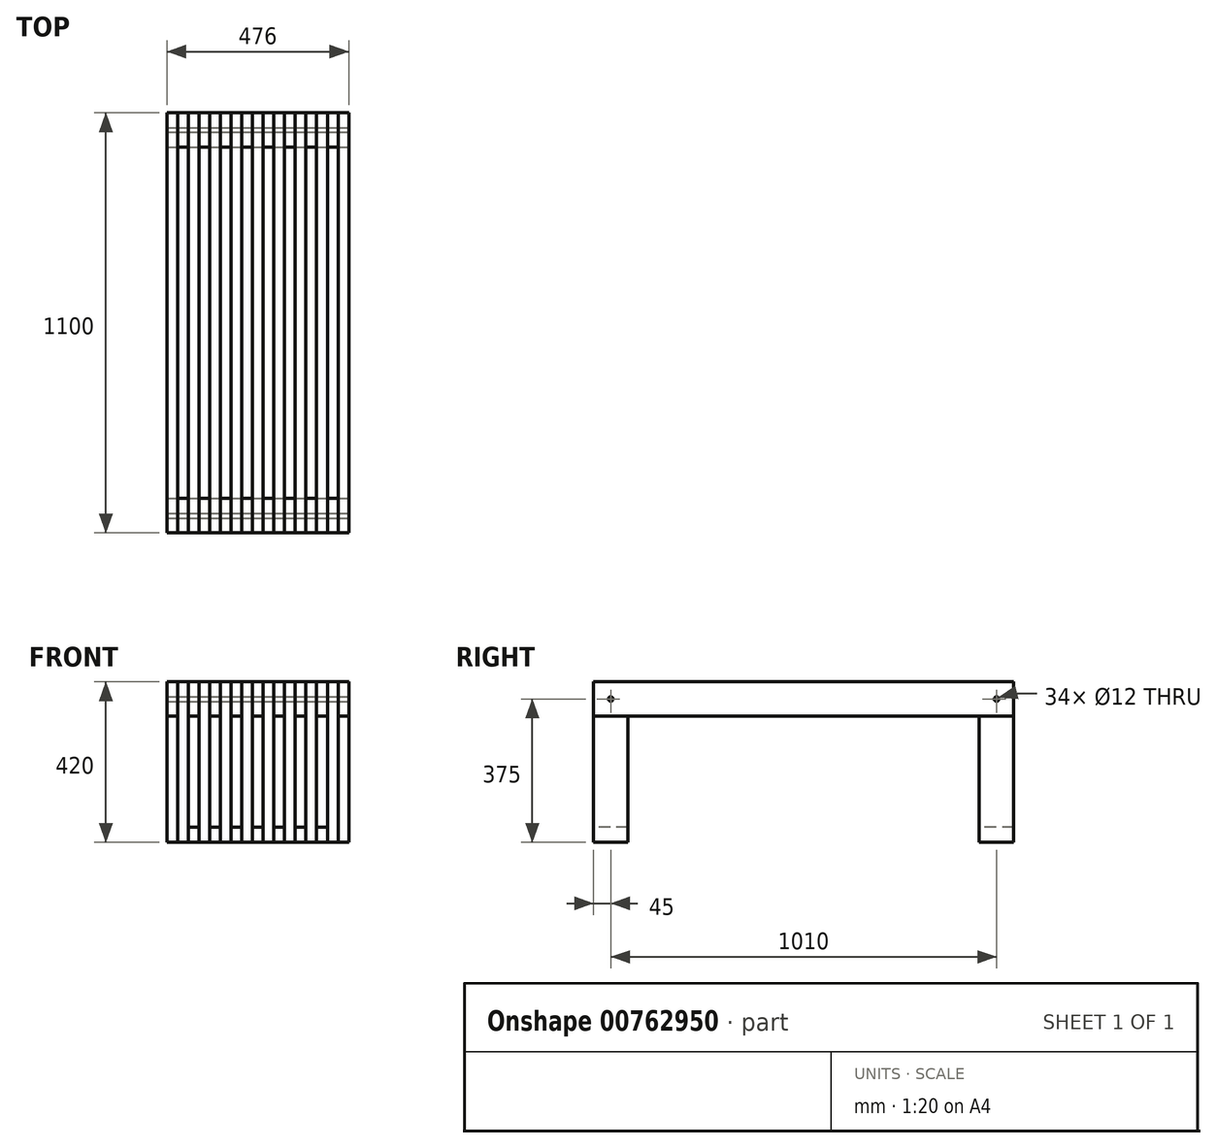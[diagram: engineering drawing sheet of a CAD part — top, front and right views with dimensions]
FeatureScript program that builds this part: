
annotation { "Feature Type Name" : "Feature", "Feature Type Description" : "" }
export const myFeature = defineFeature(function(context is Context, id is Id, definition is map)
    precondition{}
    {
        {
            var Q0;
            Q0=qCreatedBy(makeId("Front.planeOp"),FACE);
            var sketch = newSketch(context, id + "F0", { "sketchPlane" : qUnion([Q0])});
            skLineSegment(sketch, "E0.bottom", {"start": v(0, 0) * mm, "end": v(28, 0) * mm});
            skLineSegment(sketch, "E0.top", {"start": v(0, 90) * mm, "end": v(28, 90) * mm});
            skLineSegment(sketch, "E0.left", {"start": v(0, 0) * mm, "end": v(0, 90) * mm});
            skLineSegment(sketch, "E0.right", {"start": v(28, 0) * mm, "end": v(28, 90) * mm});
            skLineSegment(sketch, "E1.1.0.0", {"start": v(56, 90) * mm, "end": v(84, 90) * mm});
            skLineSegment(sketch, "E1.1.0.1", {"start": v(56, 0) * mm, "end": v(56, 90) * mm});
            skLineSegment(sketch, "E1.1.0.2", {"start": v(84, 0) * mm, "end": v(84, 90) * mm});
            skLineSegment(sketch, "E1.1.0.3", {"start": v(56, 0) * mm, "end": v(84, 0) * mm});
            skLineSegment(sketch, "E1.2.0.0", {"start": v(112, 90) * mm, "end": v(140, 90) * mm});
            skLineSegment(sketch, "E1.2.0.1", {"start": v(112, 0) * mm, "end": v(112, 90) * mm});
            skLineSegment(sketch, "E1.2.0.2", {"start": v(140, 0) * mm, "end": v(140, 90) * mm});
            skLineSegment(sketch, "E1.2.0.3", {"start": v(112, 0) * mm, "end": v(140, 0) * mm});
            skLineSegment(sketch, "E1.3.0.0", {"start": v(168, 90) * mm, "end": v(196, 90) * mm});
            skLineSegment(sketch, "E1.3.0.1", {"start": v(168, 0) * mm, "end": v(168, 90) * mm});
            skLineSegment(sketch, "E1.3.0.2", {"start": v(196, 0) * mm, "end": v(196, 90) * mm});
            skLineSegment(sketch, "E1.3.0.3", {"start": v(168, 0) * mm, "end": v(196, 0) * mm});
            skLineSegment(sketch, "E1.4.0.0", {"start": v(224, 90) * mm, "end": v(252, 90) * mm});
            skLineSegment(sketch, "E1.4.0.1", {"start": v(224, 0) * mm, "end": v(224, 90) * mm});
            skLineSegment(sketch, "E1.4.0.2", {"start": v(252, 0) * mm, "end": v(252, 90) * mm});
            skLineSegment(sketch, "E1.4.0.3", {"start": v(224, 0) * mm, "end": v(252, 0) * mm});
            skLineSegment(sketch, "E1.5.0.0", {"start": v(280, 90) * mm, "end": v(308, 90) * mm});
            skLineSegment(sketch, "E1.5.0.1", {"start": v(280, 0) * mm, "end": v(280, 90) * mm});
            skLineSegment(sketch, "E1.5.0.2", {"start": v(308, 0) * mm, "end": v(308, 90) * mm});
            skLineSegment(sketch, "E1.5.0.3", {"start": v(280, 0) * mm, "end": v(308, 0) * mm});
            skLineSegment(sketch, "E1.6.0.0", {"start": v(336, 90) * mm, "end": v(364, 90) * mm});
            skLineSegment(sketch, "E1.6.0.1", {"start": v(336, 0) * mm, "end": v(336, 90) * mm});
            skLineSegment(sketch, "E1.6.0.2", {"start": v(364, 0) * mm, "end": v(364, 90) * mm});
            skLineSegment(sketch, "E1.6.0.3", {"start": v(336, 0) * mm, "end": v(364, 0) * mm});
            skLineSegment(sketch, "E1.7.0.0", {"start": v(392, 90) * mm, "end": v(420, 90) * mm});
            skLineSegment(sketch, "E1.7.0.1", {"start": v(392, 0) * mm, "end": v(392, 90) * mm});
            skLineSegment(sketch, "E1.7.0.2", {"start": v(420, 0) * mm, "end": v(420, 90) * mm});
            skLineSegment(sketch, "E1.7.0.3", {"start": v(392, 0) * mm, "end": v(420, 0) * mm});
            skLineSegment(sketch, "E1.direction1", {"start": v(0, 0) * mm, "end": v(56, 0) * mm, "construction": true});
            skLineSegment(sketch, "E2.0.8.0", {"start": v(448, 90) * mm, "end": v(476, 90) * mm});
            skLineSegment(sketch, "E2.3.8.0", {"start": v(448, 0) * mm, "end": v(448, 90) * mm});
            skLineSegment(sketch, "E2.6.8.0", {"start": v(476, 0) * mm, "end": v(476, 90) * mm});
            skLineSegment(sketch, "E2.9.8.0", {"start": v(448, 0) * mm, "end": v(476, 0) * mm});
            skSolve(sketch);
        }
        {
            var Q0;
            Q0=makeQuery(id+"F0.imprint","IMPRINT",FACE,{"disambiguationData":[TD([[makeQuery(id+"F0.imprint","IMPRINT",EDGE,{"derivedFrom":sQuery(id+"F0.wireOp",EDGE,"E0.bottom")}),1.0]])]});
            var Q1;
            Q1=makeQuery(id+"F0.imprint","IMPRINT",FACE,{"disambiguationData":[TD([[makeQuery(id+"F0.imprint","IMPRINT",EDGE,{"derivedFrom":sQuery(id+"F0.wireOp",EDGE,"E1.1.0.0")}),-1.0]])]});
            var Q2;
            Q2=makeQuery(id+"F0.imprint","IMPRINT",FACE,{"disambiguationData":[TD([[makeQuery(id+"F0.imprint","IMPRINT",EDGE,{"derivedFrom":sQuery(id+"F0.wireOp",EDGE,"E1.2.0.0")}),-1.0]])]});
            var Q3;
            Q3=makeQuery(id+"F0.imprint","IMPRINT",FACE,{"disambiguationData":[TD([[makeQuery(id+"F0.imprint","IMPRINT",EDGE,{"derivedFrom":sQuery(id+"F0.wireOp",EDGE,"E1.3.0.0")}),-1.0]])]});
            var Q4;
            Q4=makeQuery(id+"F0.imprint","IMPRINT",FACE,{"disambiguationData":[TD([[makeQuery(id+"F0.imprint","IMPRINT",EDGE,{"derivedFrom":sQuery(id+"F0.wireOp",EDGE,"E1.4.0.0")}),-1.0]])]});
            var Q5;
            Q5=makeQuery(id+"F0.imprint","IMPRINT",FACE,{"disambiguationData":[TD([[makeQuery(id+"F0.imprint","IMPRINT",EDGE,{"derivedFrom":sQuery(id+"F0.wireOp",EDGE,"E1.5.0.0")}),-1.0]])]});
            var Q6;
            Q6=makeQuery(id+"F0.imprint","IMPRINT",FACE,{"disambiguationData":[TD([[makeQuery(id+"F0.imprint","IMPRINT",EDGE,{"derivedFrom":sQuery(id+"F0.wireOp",EDGE,"E1.6.0.0")}),-1.0]])]});
            var Q7;
            Q7=makeQuery(id+"F0.imprint","IMPRINT",FACE,{"disambiguationData":[TD([[makeQuery(id+"F0.imprint","IMPRINT",EDGE,{"derivedFrom":sQuery(id+"F0.wireOp",EDGE,"E1.7.0.0")}),-1.0]])]});
            var Q8;
            Q8=makeQuery(id+"F0.imprint","IMPRINT",FACE,{"disambiguationData":[TD([[makeQuery(id+"F0.imprint","IMPRINT",EDGE,{"derivedFrom":sQuery(id+"F0.wireOp",EDGE,"E2.0.8.0")}),-1.0]])]});
            extrude(context, id + "F1", {"entities" : qUnion([Q0, Q1, Q2, Q3, Q4, Q5, Q6, Q7, Q8]), "depth" : 1100 * mm, "offsetDistance" : 25 * mm});
        }
        {
            var Q0;
            Q0=qCreatedBy(makeId("Top.planeOp"),FACE);
            var sketch = newSketch(context, id + "F2", { "sketchPlane" : qUnion([Q0])});
            skLineSegment(sketch, "E3.bottom", {"start": v(28, 0) * mm, "end": v(56, 0) * mm});
            skLineSegment(sketch, "E3.top", {"start": v(28, -90) * mm, "end": v(56, -90) * mm});
            skLineSegment(sketch, "E3.left", {"start": v(28, 0) * mm, "end": v(28, -90) * mm});
            skLineSegment(sketch, "E3.right", {"start": v(56, 0) * mm, "end": v(56, -90) * mm});
            skLineSegment(sketch, "E4.0.1.0", {"start": v(28, -1010) * mm, "end": v(56, -1010) * mm});
            skLineSegment(sketch, "E4.0.1.1", {"start": v(28, -1100) * mm, "end": v(56, -1100) * mm});
            skLineSegment(sketch, "E4.0.1.2", {"start": v(28, -1010) * mm, "end": v(28, -1100) * mm});
            skLineSegment(sketch, "E4.0.1.3", {"start": v(56, -1010) * mm, "end": v(56, -1100) * mm});
            skLineSegment(sketch, "E4.1.0.0", {"start": v(84, 0) * mm, "end": v(112, 0) * mm});
            skLineSegment(sketch, "E4.1.0.1", {"start": v(84, -90) * mm, "end": v(112, -90) * mm});
            skLineSegment(sketch, "E4.1.0.2", {"start": v(84, 0) * mm, "end": v(84, -90) * mm});
            skLineSegment(sketch, "E4.1.0.3", {"start": v(112, 0) * mm, "end": v(112, -90) * mm});
            skLineSegment(sketch, "E4.1.1.0", {"start": v(84, -1010) * mm, "end": v(112, -1010) * mm});
            skLineSegment(sketch, "E4.1.1.1", {"start": v(84, -1100) * mm, "end": v(112, -1100) * mm});
            skLineSegment(sketch, "E4.1.1.2", {"start": v(84, -1010) * mm, "end": v(84, -1100) * mm});
            skLineSegment(sketch, "E4.1.1.3", {"start": v(112, -1010) * mm, "end": v(112, -1100) * mm});
            skLineSegment(sketch, "E4.2.0.0", {"start": v(140, 0) * mm, "end": v(168, 0) * mm});
            skLineSegment(sketch, "E4.2.0.1", {"start": v(140, -90) * mm, "end": v(168, -90) * mm});
            skLineSegment(sketch, "E4.2.0.2", {"start": v(140, 0) * mm, "end": v(140, -90) * mm});
            skLineSegment(sketch, "E4.2.0.3", {"start": v(168, 0) * mm, "end": v(168, -90) * mm});
            skLineSegment(sketch, "E4.2.1.0", {"start": v(140, -1010) * mm, "end": v(168, -1010) * mm});
            skLineSegment(sketch, "E4.2.1.1", {"start": v(140, -1100) * mm, "end": v(168, -1100) * mm});
            skLineSegment(sketch, "E4.2.1.2", {"start": v(140, -1010) * mm, "end": v(140, -1100) * mm});
            skLineSegment(sketch, "E4.2.1.3", {"start": v(168, -1010) * mm, "end": v(168, -1100) * mm});
            skLineSegment(sketch, "E4.3.0.0", {"start": v(196, 0) * mm, "end": v(224, 0) * mm});
            skLineSegment(sketch, "E4.3.0.1", {"start": v(196, -90) * mm, "end": v(224, -90) * mm});
            skLineSegment(sketch, "E4.3.0.2", {"start": v(196, 0) * mm, "end": v(196, -90) * mm});
            skLineSegment(sketch, "E4.3.0.3", {"start": v(224, 0) * mm, "end": v(224, -90) * mm});
            skLineSegment(sketch, "E4.3.1.0", {"start": v(196, -1010) * mm, "end": v(224, -1010) * mm});
            skLineSegment(sketch, "E4.3.1.1", {"start": v(196, -1100) * mm, "end": v(224, -1100) * mm});
            skLineSegment(sketch, "E4.3.1.2", {"start": v(196, -1010) * mm, "end": v(196, -1100) * mm});
            skLineSegment(sketch, "E4.3.1.3", {"start": v(224, -1010) * mm, "end": v(224, -1100) * mm});
            skLineSegment(sketch, "E4.4.0.0", {"start": v(252, 0) * mm, "end": v(280, 0) * mm});
            skLineSegment(sketch, "E4.4.0.1", {"start": v(252, -90) * mm, "end": v(280, -90) * mm});
            skLineSegment(sketch, "E4.4.0.2", {"start": v(252, 0) * mm, "end": v(252, -90) * mm});
            skLineSegment(sketch, "E4.4.0.3", {"start": v(280, 0) * mm, "end": v(280, -90) * mm});
            skLineSegment(sketch, "E4.4.1.0", {"start": v(252, -1010) * mm, "end": v(280, -1010) * mm});
            skLineSegment(sketch, "E4.4.1.1", {"start": v(252, -1100) * mm, "end": v(280, -1100) * mm});
            skLineSegment(sketch, "E4.4.1.2", {"start": v(252, -1010) * mm, "end": v(252, -1100) * mm});
            skLineSegment(sketch, "E4.4.1.3", {"start": v(280, -1010) * mm, "end": v(280, -1100) * mm});
            skLineSegment(sketch, "E4.5.0.0", {"start": v(308, 0) * mm, "end": v(336, 0) * mm});
            skLineSegment(sketch, "E4.5.0.1", {"start": v(308, -90) * mm, "end": v(336, -90) * mm});
            skLineSegment(sketch, "E4.5.0.2", {"start": v(308, 0) * mm, "end": v(308, -90) * mm});
            skLineSegment(sketch, "E4.5.0.3", {"start": v(336, 0) * mm, "end": v(336, -90) * mm});
            skLineSegment(sketch, "E4.5.1.0", {"start": v(308, -1010) * mm, "end": v(336, -1010) * mm});
            skLineSegment(sketch, "E4.5.1.1", {"start": v(308, -1100) * mm, "end": v(336, -1100) * mm});
            skLineSegment(sketch, "E4.5.1.2", {"start": v(308, -1010) * mm, "end": v(308, -1100) * mm});
            skLineSegment(sketch, "E4.5.1.3", {"start": v(336, -1010) * mm, "end": v(336, -1100) * mm});
            skLineSegment(sketch, "E4.6.0.0", {"start": v(364, 0) * mm, "end": v(392, 0) * mm});
            skLineSegment(sketch, "E4.6.0.1", {"start": v(364, -90) * mm, "end": v(392, -90) * mm});
            skLineSegment(sketch, "E4.6.0.2", {"start": v(364, 0) * mm, "end": v(364, -90) * mm});
            skLineSegment(sketch, "E4.6.0.3", {"start": v(392, 0) * mm, "end": v(392, -90) * mm});
            skLineSegment(sketch, "E4.6.1.0", {"start": v(364, -1010) * mm, "end": v(392, -1010) * mm});
            skLineSegment(sketch, "E4.6.1.1", {"start": v(364, -1100) * mm, "end": v(392, -1100) * mm});
            skLineSegment(sketch, "E4.6.1.2", {"start": v(364, -1010) * mm, "end": v(364, -1100) * mm});
            skLineSegment(sketch, "E4.6.1.3", {"start": v(392, -1010) * mm, "end": v(392, -1100) * mm});
            skLineSegment(sketch, "E4.7.0.0", {"start": v(420, 0) * mm, "end": v(448, 0) * mm});
            skLineSegment(sketch, "E4.7.0.1", {"start": v(420, -90) * mm, "end": v(448, -90) * mm});
            skLineSegment(sketch, "E4.7.0.2", {"start": v(420, 0) * mm, "end": v(420, -90) * mm});
            skLineSegment(sketch, "E4.7.0.3", {"start": v(448, 0) * mm, "end": v(448, -90) * mm});
            skLineSegment(sketch, "E4.7.1.0", {"start": v(420, -1010) * mm, "end": v(448, -1010) * mm});
            skLineSegment(sketch, "E4.7.1.1", {"start": v(420, -1100) * mm, "end": v(448, -1100) * mm});
            skLineSegment(sketch, "E4.7.1.2", {"start": v(420, -1010) * mm, "end": v(420, -1100) * mm});
            skLineSegment(sketch, "E4.7.1.3", {"start": v(448, -1010) * mm, "end": v(448, -1100) * mm});
            skLineSegment(sketch, "E4.direction1", {"start": v(28, -90) * mm, "end": v(84, -90) * mm, "construction": true});
            skLineSegment(sketch, "E4.direction2", {"start": v(28, -90) * mm, "end": v(28, -1100) * mm, "construction": true});
            skSolve(sketch);
        }
        {
            var Q0;
            Q0 = qSketchRegion(id + "F2", true);
            extrude(context, id + "F3", {"entities" : qUnion([Q0]), "depth" : 90 * mm, "offsetDistance" : 25 * mm, "hasSecondDirection" : true, "secondDirectionOppositeDirection" : true, "secondDirectionDepth" : 330 * mm});
        }
        {
            var Q0;
            Q0=makeQuery(id+"F3.opExtrude","CAP_FACE",FACE,{"disambiguationData":[OSD([sQuery(id+"F2.wireOp",EDGE,"E3.bottom"),sQuery(id+"F2.wireOp",EDGE,"E3.top"),sQuery(id+"F2.wireOp",EDGE,"E3.left"),sQuery(id+"F2.wireOp",EDGE,"E3.right")])],"isStart":true});
            cPlane(context, id + "F4", {"entities" : qUnion([Q0]), "cplaneType" : CPlaneType.OFFSET, "offset" : 0 * mm, "oppositeDirection" : true, "width" : 150 * mm, "height" : 150 * mm});
        }
        {
            var Q0;
            Q0=qCreatedBy(id+"F4.planeOp",FACE);
            var sketch = newSketch(context, id + "F5", { "sketchPlane" : qUnion([Q0])});
            skLineSegment(sketch, "E5.bottom", {"start": v(56, 0) * mm, "end": v(84, 0) * mm});
            skLineSegment(sketch, "E5.top", {"start": v(56, 90) * mm, "end": v(84, 90) * mm});
            skLineSegment(sketch, "E5.left", {"start": v(56, 0) * mm, "end": v(56, 90) * mm});
            skLineSegment(sketch, "E5.right", {"start": v(84, 0) * mm, "end": v(84, 90) * mm});
            skLineSegment(sketch, "E6.0.1.0", {"start": v(56, 1010) * mm, "end": v(84, 1010) * mm});
            skLineSegment(sketch, "E6.0.1.1", {"start": v(56, 1100) * mm, "end": v(84, 1100) * mm});
            skLineSegment(sketch, "E6.0.1.2", {"start": v(56, 1010) * mm, "end": v(56, 1100) * mm});
            skLineSegment(sketch, "E6.0.1.3", {"start": v(84, 1010) * mm, "end": v(84, 1100) * mm});
            skLineSegment(sketch, "E6.1.0.0", {"start": v(112, 0) * mm, "end": v(140, 0) * mm});
            skLineSegment(sketch, "E6.1.0.1", {"start": v(112, 90) * mm, "end": v(140, 90) * mm});
            skLineSegment(sketch, "E6.1.0.2", {"start": v(112, 0) * mm, "end": v(112, 90) * mm});
            skLineSegment(sketch, "E6.1.0.3", {"start": v(140, 0) * mm, "end": v(140, 90) * mm});
            skLineSegment(sketch, "E6.1.1.0", {"start": v(112, 1010) * mm, "end": v(140, 1010) * mm});
            skLineSegment(sketch, "E6.1.1.1", {"start": v(112, 1100) * mm, "end": v(140, 1100) * mm});
            skLineSegment(sketch, "E6.1.1.2", {"start": v(112, 1010) * mm, "end": v(112, 1100) * mm});
            skLineSegment(sketch, "E6.1.1.3", {"start": v(140, 1010) * mm, "end": v(140, 1100) * mm});
            skLineSegment(sketch, "E6.2.0.0", {"start": v(168, 0) * mm, "end": v(196, 0) * mm});
            skLineSegment(sketch, "E6.2.0.1", {"start": v(168, 90) * mm, "end": v(196, 90) * mm});
            skLineSegment(sketch, "E6.2.0.2", {"start": v(168, 0) * mm, "end": v(168, 90) * mm});
            skLineSegment(sketch, "E6.2.0.3", {"start": v(196, 0) * mm, "end": v(196, 90) * mm});
            skLineSegment(sketch, "E6.2.1.0", {"start": v(168, 1010) * mm, "end": v(196, 1010) * mm});
            skLineSegment(sketch, "E6.2.1.1", {"start": v(168, 1100) * mm, "end": v(196, 1100) * mm});
            skLineSegment(sketch, "E6.2.1.2", {"start": v(168, 1010) * mm, "end": v(168, 1100) * mm});
            skLineSegment(sketch, "E6.2.1.3", {"start": v(196, 1010) * mm, "end": v(196, 1100) * mm});
            skLineSegment(sketch, "E6.3.0.0", {"start": v(224, 0) * mm, "end": v(252, 0) * mm});
            skLineSegment(sketch, "E6.3.0.1", {"start": v(224, 90) * mm, "end": v(252, 90) * mm});
            skLineSegment(sketch, "E6.3.0.2", {"start": v(224, 0) * mm, "end": v(224, 90) * mm});
            skLineSegment(sketch, "E6.3.0.3", {"start": v(252, 0) * mm, "end": v(252, 90) * mm});
            skLineSegment(sketch, "E6.3.1.0", {"start": v(224, 1010) * mm, "end": v(252, 1010) * mm});
            skLineSegment(sketch, "E6.3.1.1", {"start": v(224, 1100) * mm, "end": v(252, 1100) * mm});
            skLineSegment(sketch, "E6.3.1.2", {"start": v(224, 1010) * mm, "end": v(224, 1100) * mm});
            skLineSegment(sketch, "E6.3.1.3", {"start": v(252, 1010) * mm, "end": v(252, 1100) * mm});
            skLineSegment(sketch, "E6.4.0.0", {"start": v(280, 0) * mm, "end": v(308, 0) * mm});
            skLineSegment(sketch, "E6.4.0.1", {"start": v(280, 90) * mm, "end": v(308, 90) * mm});
            skLineSegment(sketch, "E6.4.0.2", {"start": v(280, 0) * mm, "end": v(280, 90) * mm});
            skLineSegment(sketch, "E6.4.0.3", {"start": v(308, 0) * mm, "end": v(308, 90) * mm});
            skLineSegment(sketch, "E6.4.1.0", {"start": v(280, 1010) * mm, "end": v(308, 1010) * mm});
            skLineSegment(sketch, "E6.4.1.1", {"start": v(280, 1100) * mm, "end": v(308, 1100) * mm});
            skLineSegment(sketch, "E6.4.1.2", {"start": v(280, 1010) * mm, "end": v(280, 1100) * mm});
            skLineSegment(sketch, "E6.4.1.3", {"start": v(308, 1010) * mm, "end": v(308, 1100) * mm});
            skLineSegment(sketch, "E6.5.0.0", {"start": v(336, 0) * mm, "end": v(364, 0) * mm});
            skLineSegment(sketch, "E6.5.0.1", {"start": v(336, 90) * mm, "end": v(364, 90) * mm});
            skLineSegment(sketch, "E6.5.0.2", {"start": v(336, 0) * mm, "end": v(336, 90) * mm});
            skLineSegment(sketch, "E6.5.0.3", {"start": v(364, 0) * mm, "end": v(364, 90) * mm});
            skLineSegment(sketch, "E6.5.1.0", {"start": v(336, 1010) * mm, "end": v(364, 1010) * mm});
            skLineSegment(sketch, "E6.5.1.1", {"start": v(336, 1100) * mm, "end": v(364, 1100) * mm});
            skLineSegment(sketch, "E6.5.1.2", {"start": v(336, 1010) * mm, "end": v(336, 1100) * mm});
            skLineSegment(sketch, "E6.5.1.3", {"start": v(364, 1010) * mm, "end": v(364, 1100) * mm});
            skLineSegment(sketch, "E6.6.0.0", {"start": v(392, 0) * mm, "end": v(420, 0) * mm});
            skLineSegment(sketch, "E6.6.0.1", {"start": v(392, 90) * mm, "end": v(420, 90) * mm});
            skLineSegment(sketch, "E6.6.0.2", {"start": v(392, 0) * mm, "end": v(392, 90) * mm});
            skLineSegment(sketch, "E6.6.0.3", {"start": v(420, 0) * mm, "end": v(420, 90) * mm});
            skLineSegment(sketch, "E6.6.1.0", {"start": v(392, 1010) * mm, "end": v(420, 1010) * mm});
            skLineSegment(sketch, "E6.6.1.1", {"start": v(392, 1100) * mm, "end": v(420, 1100) * mm});
            skLineSegment(sketch, "E6.6.1.2", {"start": v(392, 1010) * mm, "end": v(392, 1100) * mm});
            skLineSegment(sketch, "E6.6.1.3", {"start": v(420, 1010) * mm, "end": v(420, 1100) * mm});
            skLineSegment(sketch, "E6.direction1", {"start": v(56, 0) * mm, "end": v(112, 0) * mm, "construction": true});
            skLineSegment(sketch, "E6.direction2", {"start": v(56, 0) * mm, "end": v(56, 1010) * mm, "construction": true});
            skSolve(sketch);
        }
        {
            var Q0;
            Q0 = qSketchRegion(id + "F5", true);
            extrude(context, id + "F6", {"entities" : qUnion([Q0]), "oppositeDirection" : true, "depth" : 40 * mm, "offsetDistance" : 25 * mm});
        }
        {
            var Q0;
            Q0=qCreatedBy(makeId("Right.planeOp"),FACE);
            var sketch = newSketch(context, id + "F7", { "sketchPlane" : qUnion([Q0])});
            skCircle(sketch, "E7", {"center": v(-45, 45) * mm, "radius": 6 * mm});
            skCircle(sketch, "E8.1.0.0", {"center": v(-1055, 45) * mm, "radius": 6 * mm});
            skLineSegment(sketch, "E8.direction1", {"start": v(-45, 45) * mm, "end": v(-1055, 45) * mm, "construction": true});
            skSolve(sketch);
        }
        {
            var Q0;
            Q0=sQuery(id+"F7.wireOp",VERTEX,"E8.direction1.start");
            var Q1;
            Q1=sQuery(id+"F7.wireOp",VERTEX,"E8.direction1.end");
            var Q2;
            Q2=makeQuery(id+"F1.opExtrude","SWEPT_BODY",BODY,{"disambiguationData":[OSD([sQuery(id+"F0.wireOp",EDGE,"E0.bottom"),sQuery(id+"F0.wireOp",EDGE,"E0.top"),sQuery(id+"F0.wireOp",EDGE,"E0.left"),sQuery(id+"F0.wireOp",EDGE,"E0.right")])]});
            var Q3;
            Q3=makeQuery(id+"F1.opExtrude","SWEPT_BODY",BODY,{"disambiguationData":[OSD([sQuery(id+"F0.wireOp",EDGE,"E1.1.0.0"),sQuery(id+"F0.wireOp",EDGE,"E1.1.0.1"),sQuery(id+"F0.wireOp",EDGE,"E1.1.0.2"),sQuery(id+"F0.wireOp",EDGE,"E1.1.0.3")])]});
            var Q4;
            Q4=makeQuery(id+"F1.opExtrude","SWEPT_BODY",BODY,{"disambiguationData":[OSD([sQuery(id+"F0.wireOp",EDGE,"E1.2.0.0"),sQuery(id+"F0.wireOp",EDGE,"E1.2.0.1"),sQuery(id+"F0.wireOp",EDGE,"E1.2.0.2"),sQuery(id+"F0.wireOp",EDGE,"E1.2.0.3")])]});
            var Q5;
            Q5=makeQuery(id+"F1.opExtrude","SWEPT_BODY",BODY,{"disambiguationData":[OSD([sQuery(id+"F0.wireOp",EDGE,"E1.3.0.0"),sQuery(id+"F0.wireOp",EDGE,"E1.3.0.1"),sQuery(id+"F0.wireOp",EDGE,"E1.3.0.2"),sQuery(id+"F0.wireOp",EDGE,"E1.3.0.3")])]});
            var Q6;
            Q6=makeQuery(id+"F1.opExtrude","SWEPT_BODY",BODY,{"disambiguationData":[OSD([sQuery(id+"F0.wireOp",EDGE,"E1.4.0.0"),sQuery(id+"F0.wireOp",EDGE,"E1.4.0.1"),sQuery(id+"F0.wireOp",EDGE,"E1.4.0.2"),sQuery(id+"F0.wireOp",EDGE,"E1.4.0.3")])]});
            var Q7;
            Q7=makeQuery(id+"F1.opExtrude","SWEPT_BODY",BODY,{"disambiguationData":[OSD([sQuery(id+"F0.wireOp",EDGE,"E1.5.0.0"),sQuery(id+"F0.wireOp",EDGE,"E1.5.0.1"),sQuery(id+"F0.wireOp",EDGE,"E1.5.0.2"),sQuery(id+"F0.wireOp",EDGE,"E1.5.0.3")])]});
            var Q8;
            Q8=makeQuery(id+"F1.opExtrude","SWEPT_BODY",BODY,{"disambiguationData":[OSD([sQuery(id+"F0.wireOp",EDGE,"E1.6.0.0"),sQuery(id+"F0.wireOp",EDGE,"E1.6.0.1"),sQuery(id+"F0.wireOp",EDGE,"E1.6.0.2"),sQuery(id+"F0.wireOp",EDGE,"E1.6.0.3")])]});
            var Q9;
            Q9=makeQuery(id+"F1.opExtrude","SWEPT_BODY",BODY,{"disambiguationData":[OSD([sQuery(id+"F0.wireOp",EDGE,"E1.7.0.0"),sQuery(id+"F0.wireOp",EDGE,"E1.7.0.1"),sQuery(id+"F0.wireOp",EDGE,"E1.7.0.2"),sQuery(id+"F0.wireOp",EDGE,"E1.7.0.3")])]});
            var Q10;
            Q10=makeQuery(id+"F1.opExtrude","SWEPT_BODY",BODY,{"disambiguationData":[OSD([sQuery(id+"F0.wireOp",EDGE,"E2.0.8.0"),sQuery(id+"F0.wireOp",EDGE,"E2.3.8.0"),sQuery(id+"F0.wireOp",EDGE,"E2.6.8.0"),sQuery(id+"F0.wireOp",EDGE,"E2.9.8.0")])]});
            var Q11;
            Q11=makeQuery(id+"F3.opExtrude","SWEPT_BODY",BODY,{"disambiguationData":[OSD([sQuery(id+"F2.wireOp",EDGE,"E3.bottom"),sQuery(id+"F2.wireOp",EDGE,"E3.top"),sQuery(id+"F2.wireOp",EDGE,"E3.left"),sQuery(id+"F2.wireOp",EDGE,"E3.right")])]});
            var Q12;
            Q12=makeQuery(id+"F3.opExtrude","SWEPT_BODY",BODY,{"disambiguationData":[OSD([sQuery(id+"F2.wireOp",EDGE,"E4.1.0.0"),sQuery(id+"F2.wireOp",EDGE,"E4.1.0.1"),sQuery(id+"F2.wireOp",EDGE,"E4.1.0.2"),sQuery(id+"F2.wireOp",EDGE,"E4.1.0.3")])]});
            var Q13;
            Q13=makeQuery(id+"F3.opExtrude","SWEPT_BODY",BODY,{"disambiguationData":[OSD([sQuery(id+"F2.wireOp",EDGE,"E4.2.0.0"),sQuery(id+"F2.wireOp",EDGE,"E4.2.0.1"),sQuery(id+"F2.wireOp",EDGE,"E4.2.0.2"),sQuery(id+"F2.wireOp",EDGE,"E4.2.0.3")])]});
            var Q14;
            Q14=makeQuery(id+"F3.opExtrude","SWEPT_BODY",BODY,{"disambiguationData":[OSD([sQuery(id+"F2.wireOp",EDGE,"E4.3.0.0"),sQuery(id+"F2.wireOp",EDGE,"E4.3.0.1"),sQuery(id+"F2.wireOp",EDGE,"E4.3.0.2"),sQuery(id+"F2.wireOp",EDGE,"E4.3.0.3")])]});
            var Q15;
            Q15=makeQuery(id+"F3.opExtrude","SWEPT_BODY",BODY,{"disambiguationData":[OSD([sQuery(id+"F2.wireOp",EDGE,"E4.4.0.0"),sQuery(id+"F2.wireOp",EDGE,"E4.4.0.1"),sQuery(id+"F2.wireOp",EDGE,"E4.4.0.2"),sQuery(id+"F2.wireOp",EDGE,"E4.4.0.3")])]});
            var Q16;
            Q16=makeQuery(id+"F3.opExtrude","SWEPT_BODY",BODY,{"disambiguationData":[OSD([sQuery(id+"F2.wireOp",EDGE,"E4.5.0.0"),sQuery(id+"F2.wireOp",EDGE,"E4.5.0.1"),sQuery(id+"F2.wireOp",EDGE,"E4.5.0.2"),sQuery(id+"F2.wireOp",EDGE,"E4.5.0.3")])]});
            var Q17;
            Q17=makeQuery(id+"F3.opExtrude","SWEPT_BODY",BODY,{"disambiguationData":[OSD([sQuery(id+"F2.wireOp",EDGE,"E4.6.0.0"),sQuery(id+"F2.wireOp",EDGE,"E4.6.0.1"),sQuery(id+"F2.wireOp",EDGE,"E4.6.0.2"),sQuery(id+"F2.wireOp",EDGE,"E4.6.0.3")])]});
            var Q18;
            Q18=makeQuery(id+"F3.opExtrude","SWEPT_BODY",BODY,{"disambiguationData":[OSD([sQuery(id+"F2.wireOp",EDGE,"E4.7.0.0"),sQuery(id+"F2.wireOp",EDGE,"E4.7.0.1"),sQuery(id+"F2.wireOp",EDGE,"E4.7.0.2"),sQuery(id+"F2.wireOp",EDGE,"E4.7.0.3")])]});
            var Q19;
            Q19=makeQuery(id+"F3.opExtrude","SWEPT_BODY",BODY,{"disambiguationData":[OSD([sQuery(id+"F2.wireOp",EDGE,"E4.0.1.0"),sQuery(id+"F2.wireOp",EDGE,"E4.0.1.1"),sQuery(id+"F2.wireOp",EDGE,"E4.0.1.2"),sQuery(id+"F2.wireOp",EDGE,"E4.0.1.3")])]});
            var Q20;
            Q20=makeQuery(id+"F3.opExtrude","SWEPT_BODY",BODY,{"disambiguationData":[OSD([sQuery(id+"F2.wireOp",EDGE,"E4.1.1.0"),sQuery(id+"F2.wireOp",EDGE,"E4.1.1.1"),sQuery(id+"F2.wireOp",EDGE,"E4.1.1.2"),sQuery(id+"F2.wireOp",EDGE,"E4.1.1.3")])]});
            var Q21;
            Q21=makeQuery(id+"F3.opExtrude","SWEPT_BODY",BODY,{"disambiguationData":[OSD([sQuery(id+"F2.wireOp",EDGE,"E4.2.1.0"),sQuery(id+"F2.wireOp",EDGE,"E4.2.1.1"),sQuery(id+"F2.wireOp",EDGE,"E4.2.1.2"),sQuery(id+"F2.wireOp",EDGE,"E4.2.1.3")])]});
            var Q22;
            Q22=makeQuery(id+"F3.opExtrude","SWEPT_BODY",BODY,{"disambiguationData":[OSD([sQuery(id+"F2.wireOp",EDGE,"E4.3.1.0"),sQuery(id+"F2.wireOp",EDGE,"E4.3.1.1"),sQuery(id+"F2.wireOp",EDGE,"E4.3.1.2"),sQuery(id+"F2.wireOp",EDGE,"E4.3.1.3")])]});
            var Q23;
            Q23=makeQuery(id+"F3.opExtrude","SWEPT_BODY",BODY,{"disambiguationData":[OSD([sQuery(id+"F2.wireOp",EDGE,"E4.4.1.0"),sQuery(id+"F2.wireOp",EDGE,"E4.4.1.1"),sQuery(id+"F2.wireOp",EDGE,"E4.4.1.2"),sQuery(id+"F2.wireOp",EDGE,"E4.4.1.3")])]});
            var Q24;
            Q24=makeQuery(id+"F3.opExtrude","SWEPT_BODY",BODY,{"disambiguationData":[OSD([sQuery(id+"F2.wireOp",EDGE,"E4.5.1.0"),sQuery(id+"F2.wireOp",EDGE,"E4.5.1.1"),sQuery(id+"F2.wireOp",EDGE,"E4.5.1.2"),sQuery(id+"F2.wireOp",EDGE,"E4.5.1.3")])]});
            var Q25;
            Q25=makeQuery(id+"F3.opExtrude","SWEPT_BODY",BODY,{"disambiguationData":[OSD([sQuery(id+"F2.wireOp",EDGE,"E4.6.1.0"),sQuery(id+"F2.wireOp",EDGE,"E4.6.1.1"),sQuery(id+"F2.wireOp",EDGE,"E4.6.1.2"),sQuery(id+"F2.wireOp",EDGE,"E4.6.1.3")])]});
            var Q26;
            Q26=makeQuery(id+"F3.opExtrude","SWEPT_BODY",BODY,{"disambiguationData":[OSD([sQuery(id+"F2.wireOp",EDGE,"E4.7.1.0"),sQuery(id+"F2.wireOp",EDGE,"E4.7.1.1"),sQuery(id+"F2.wireOp",EDGE,"E4.7.1.2"),sQuery(id+"F2.wireOp",EDGE,"E4.7.1.3")])]});
            hole(context, id + "F8", {"style" : HoleStyle.SIMPLE, "endStyle" : HoleEndStyle.THROUGH, "oppositeDirection" : true, "holeDiameter" : 12 * mm, "majorDiameter" : 5 * mm, "isTappedThrough" : true, "tappedDepth" : 12 * mm, "tapClearance" : 3, "locations" : qUnion([Q0, Q1]), "scope" : qUnion([Q2, Q3, Q4, Q5, Q6, Q7, Q8, Q9, Q10, Q11, Q12, Q13, Q14, Q15, Q16, Q17, Q18, Q19, Q20, Q21, Q22, Q23, Q24, Q25, Q26]), "startStyle" : HoleStartStyle.PART});
        }
        {
            var Q0;
            Q0=qCreatedBy(makeId("Top.planeOp"),FACE);
            var sketch = newSketch(context, id + "F9", { "sketchPlane" : qUnion([Q0])});
            skLineSegment(sketch, "E9.bottom", {"start": v(0, 0) * mm, "end": v(28, 0) * mm});
            skLineSegment(sketch, "E9.top", {"start": v(0, -90) * mm, "end": v(28, -90) * mm});
            skLineSegment(sketch, "E9.left", {"start": v(0, 0) * mm, "end": v(0, -90) * mm});
            skLineSegment(sketch, "E9.right", {"start": v(28, 0) * mm, "end": v(28, -90) * mm});
            skLineSegment(sketch, "E10.0.1.0", {"start": v(0, -1100) * mm, "end": v(28, -1100) * mm});
            skLineSegment(sketch, "E10.0.1.1", {"start": v(0, -1010) * mm, "end": v(0, -1100) * mm});
            skLineSegment(sketch, "E10.0.1.2", {"start": v(0, -1010) * mm, "end": v(28, -1010) * mm});
            skLineSegment(sketch, "E10.0.1.3", {"start": v(28, -1010) * mm, "end": v(28, -1100) * mm});
            skLineSegment(sketch, "E10.1.0.0", {"start": v(448, -90) * mm, "end": v(476, -90) * mm});
            skLineSegment(sketch, "E10.1.0.1", {"start": v(448, 0) * mm, "end": v(448, -90) * mm});
            skLineSegment(sketch, "E10.1.0.2", {"start": v(448, 0) * mm, "end": v(476, 0) * mm});
            skLineSegment(sketch, "E10.1.0.3", {"start": v(476, 0) * mm, "end": v(476, -90) * mm});
            skLineSegment(sketch, "E10.1.1.0", {"start": v(448, -1100) * mm, "end": v(476, -1100) * mm});
            skLineSegment(sketch, "E10.1.1.1", {"start": v(448, -1010) * mm, "end": v(448, -1100) * mm});
            skLineSegment(sketch, "E10.1.1.2", {"start": v(448, -1010) * mm, "end": v(476, -1010) * mm});
            skLineSegment(sketch, "E10.1.1.3", {"start": v(476, -1010) * mm, "end": v(476, -1100) * mm});
            skLineSegment(sketch, "E10.direction1", {"start": v(0, -90) * mm, "end": v(448, -90) * mm, "construction": true});
            skLineSegment(sketch, "E10.direction2", {"start": v(0, -90) * mm, "end": v(0, -1100) * mm, "construction": true});
            skSolve(sketch);
        }
        {
            var Q0;
            Q0 = qSketchRegion(id + "F9", true);
            extrude(context, id + "F10", {"entities" : qUnion([Q0]), "oppositeDirection" : true, "depth" : 330 * mm, "offsetDistance" : 25 * mm});
        }
    });
